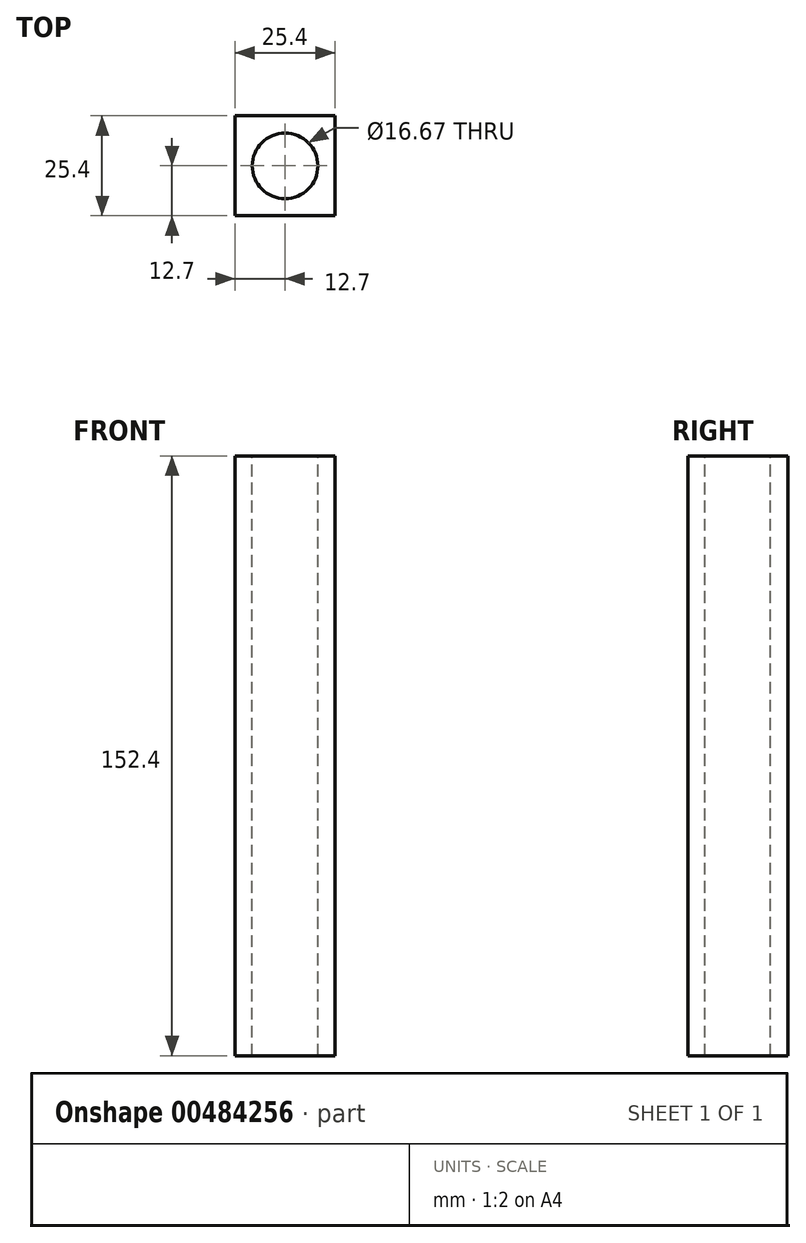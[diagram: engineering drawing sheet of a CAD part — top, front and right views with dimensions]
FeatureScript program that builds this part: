
annotation { "Feature Type Name" : "Feature", "Feature Type Description" : "" }
export const myFeature = defineFeature(function(context is Context, id is Id, definition is map)
    precondition{}
    {
        {
            var Q0;
            Q0=qCreatedBy(makeId("Top.planeOp"),FACE);
            var sketch = newSketch(context, id + "F0", { "sketchPlane" : qUnion([Q0])});
            skLineSegment(sketch, "E0.bottom", {"start": v(12.7, 12.7) * mm, "end": v(-12.7, 12.7) * mm});
            skLineSegment(sketch, "E0.top", {"start": v(12.7, -12.7) * mm, "end": v(-12.7, -12.7) * mm});
            skLineSegment(sketch, "E0.left", {"start": v(12.7, 12.7) * mm, "end": v(12.7, -12.7) * mm});
            skLineSegment(sketch, "E0.right", {"start": v(-12.7, 12.7) * mm, "end": v(-12.7, -12.7) * mm});
            skPoint(sketch, "E0.middle", {"position": v(0, 0) * mm});
            skSolve(sketch);
        }
        {
            var Q0;
            Q0=makeQuery(id+"F0.imprint","IMPRINT",FACE,{"disambiguationData":[TD([[makeQuery(id+"F0.imprint","IMPRINT",EDGE,{"derivedFrom":sQuery(id+"F0.wireOp",EDGE,"E0.bottom")}),1.0]])]});
            extrude(context, id + "F1", {"entities" : qUnion([Q0]), "depth" : 152.4 * mm});
        }
        {
            var Q0;
            Q0=makeQuery(id+"F1.opExtrude","CAP_FACE",FACE,{"disambiguationData":[OSD([sQuery(id+"F0.wireOp",EDGE,"E0.bottom"),sQuery(id+"F0.wireOp",EDGE,"E0.top"),sQuery(id+"F0.wireOp",EDGE,"E0.left"),sQuery(id+"F0.wireOp",EDGE,"E0.right")])],"isStart":false});
            var sketch = newSketch(context, id + "F2", { "sketchPlane" : qUnion([Q0])});
            skLineSegment(sketch, "E1", {"start": v(12.7, 0) * mm, "end": v(-12.7, 0) * mm});
            skPoint(sketch, "E2", {"position": v(0, 0) * mm});
            skSolve(sketch);
        }
        {
            var Q0;
            Q0=sQuery(id+"F2.wireOp",VERTEX,"E2");
            var Q1;
            Q1=makeQuery(id+"F1.opExtrude","SWEPT_BODY",BODY,{"disambiguationData":[OSD([sQuery(id+"F0.wireOp",EDGE,"E0.bottom"),sQuery(id+"F0.wireOp",EDGE,"E0.top"),sQuery(id+"F0.wireOp",EDGE,"E0.left"),sQuery(id+"F0.wireOp",EDGE,"E0.right")])]});
            hole(context, id + "F3", {"style" : HoleStyle.SIMPLE, "endStyle" : HoleEndStyle.THROUGH, "standardTappedOrClearance" : lookupTablePath({ "standard" : "ANSI", "fit" : "Normal (ASME)", "size" : "5/8", "type" : "Clearance" }), "standardBlindInLast" : lookupTablePath({ "fit" : "Free", "standard" : "ANSI", "size" : "5/8", "type" : "Clearance" }), "holeDiameter" : 16.67 * mm, "isTappedThrough" : true, "tappedDepth" : 12.7 * mm, "tapClearance" : 3, "locations" : qUnion([Q0]), "scope" : qUnion([Q1])});
        }
    });
